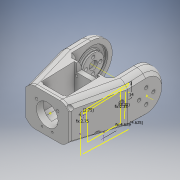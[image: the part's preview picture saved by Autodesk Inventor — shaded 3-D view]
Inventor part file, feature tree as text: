
AUTODESK INVENTOR PART (.ipt)
format: ipt  version: 2018 (Build 220112000, 112)  size: 1,030,656 bytes
history: native  units: mm
features: projected_geometry x48, sketch x44, extrude x36, hole x13, other x10, chamfer x9, fillet x7, reference x3, mirror x1, plane x1
ambient origin geometry x8: Origin, YZ Plane, XZ Plane, XY Plane, X Axis, Y Axis, Z Axis, Center Point
bodies: Solid1 (feature_tree)
feature tree (172):
  extrude  "Extrusion1"  Depth=45.0mm
  extrude  "Extrusion2"  Depth=2.25mm
  hole  "Hole1"  [1 undecoded]
  hole  "Hole2"  [1 undecoded]
  fillet  "Fillet1"  Radius=14.0mm
  extrude  "Extrusion3"  Depth=18.5mm
  extrude  "Extrusion4"  Depth=10.0mm
  extrude  "Extrusion5"  Depth=2.0mm
  extrude  "Extrusion6"  Depth=2.0mm
  hole  "Hole3"  [1 undecoded]
  extrude  "Extrusion7"  Depth=2.0mm
  extrude  "Extrusion8"  Depth=1.0mm TaperAngle=0.0deg
  extrude  "Extrusion9"  Depth=24.5mm
  extrude  "Extrusion10"  Depth=10.0mm
  extrude  "Extrusion11"  Depth=14.5mm
  extrude  "Extrusion13"  Depth=14.5mm
  extrude  "Extrusion14"  Depth=5.0mm
  extrude  "Extrusion15"  Depth=2.25mm
  extrude  "Extrusion16"  Depth=5.0mm
  extrude  "Extrusion17"  Depth=9.0mm
  chamfer  "Chamfer1"  Distance=1.0mm
  fillet  "Fillet7"  Radius=20.7mm
  fillet  "Fillet8"  Radius=32.0mm
  mirror  "Mirror1"
  sketch  "Sketch26"  dims[d55=2.25mm d56=5.0mm]
  extrude  "Extrusion24"  Depth=1.0mm TaperAngle=0.0deg
  extrude  "Extrusion25"  Depth=8.0mm
  extrude  "Extrusion26"  Depth=0.2mm TaperAngle=0.0deg
  extrude  "Extrusion27"  Depth=5.0mm TaperAngle=0.0deg
  other  "Work Axis1"
  plane  "Work Plane2"
  extrude  "Extrusion28"  Depth=0.2mm TaperAngle=0.0deg
  extrude  "Extrusion29"  Depth=2.0mm TaperAngle=45.0deg
  chamfer  "Chamfer2"  Distance=15.0mm
  extrude  "Extrusion31"  Depth=15.0mm TaperAngle=0.0deg
  chamfer  "Chamfer3"  Distance=15.0mm
  chamfer  "Chamfer4"  Distance=100.0mm
  extrude  "Extrusion32"  Depth=2.0mm TaperAngle=0.0deg
  chamfer  "Chamfer5"  Distance=6.0mm Angle=45.0deg
  extrude  "Extrusion33"  TaperAngle=0.0deg  [1 undecoded]
  sketch  "Sketch41"  dims[d100=0.2mm d101=0.0mm d102=2.5mm d103=2.0mm d104=45.0deg]
  extrude  "Extrusion34"  Depth=2.0mm
  chamfer  "Chamfer6"  Distance=11.5mm
  fillet  "Fillet9"  Radius=11.5mm
  extrude  "Extrusion35"  Depth=2.0mm TaperAngle=0.0deg
  extrude  "Extrusion36"  Depth=2.0mm TaperAngle=45.0deg
  chamfer  "Chamfer7"  Distance=2.0mm Angle=45.0deg
  fillet  "Fillet10"  Radius=7.0mm
  extrude  "Extrusion37"  Depth=2.0mm TaperAngle=0.0deg
  extrude  "Extrusion38"  Depth=2.0mm TaperAngle=45.0deg
  extrude  "Extrusion39"  Depth=2.0mm TaperAngle=0.0deg
  extrude  "Extrusion40"  Depth=2.0mm TaperAngle=0.0deg
  chamfer  "Chamfer8"  Distance=2.0mm Angle=45.0deg
  chamfer  "Chamfer9"  Distance=8.0mm
  hole  "Hole6"  [1 undecoded]
  fillet  "Fillet11"  Radius=10.970628mm
  fillet  "Fillet12"  Radius=15.470628mm
  extrude  "Extrusion41"  Depth=2.0mm TaperAngle=0.0deg
  extrude  "Extrusion42"  Depth=2.0mm TaperAngle=0.0deg
  hole  "Hole7"  [1 undecoded]
  extrude  "Extrusion43"  Depth=2.0mm
  extrude  "Extrusion44"  TaperAngle=15.0deg  [1 undecoded]
  sketch  "Sketch58"  dims[d162=5.0mm d165=100.0mm d166=0.0mm d167=100.0mm d168=0.0mm d169=6.0mm d170=2.0mm d171=45.0deg d172=0.0mm d173=11.5mm d175=11.5mm d176=11.5mm d179=100.0mm d180=0.0mm d181=5.0mm d182=2.0mm d183=45.0deg d184=5.0mm d185=2.0mm d186=45.0deg d187=7.0mm d188=100.0mm d189=0.0mm d190=5.0mm d191=2.0mm d192=45.0deg d193=100.0mm d194=0.0mm d195=100.0mm d196=0.0mm d197=5.0mm d198=2.0mm d199=45.0deg d200=8.0mm d202=15.0deg d204=10.970628mm d205=15.470628mm d206=2.5mm d207=0.0mm d208=2.5mm d209=0.0mm d210=3.0mm d211=2.0mm d212=45.0deg d213=2.0mm d215=15.0deg d216=4.0mm d217=4.0mm d218=5.0mm d219=0.0mm d222=32.0mm d223=4.0mm d224=0.0mm d225=2.5mm d226=0.0mm d227=6.5mm d228=0.0mm d229=3.0mm d230=2.0mm d231=45.0deg d232=3.0mm d233=2.0mm d234=45.0deg d235=1.567mm d236=15.0mm d237=4.0mm d238=2.0mm d239=90.0deg d240=15.0mm d241=20.594885mm d242=2.0mm d243=0.75mm d244=20.5mm d245=3.05mm d246=0.0mm d247=14.0mm d248=3.2mm d249=6.0mm d250=4.0mm d251=2.0mm d252=90.0deg d253=8.8mm d254=20.594885mm d255=20.5mm d256=1.55mm d257=0.0mm d258=8.0mm d259=2.5mm d260=0.0mm d261=8.0mm d262=2.5mm d263=0.0mm d266=4.624622mm d267=4.624622mm d268=2.75mm d269=2.75mm d270=2.35mm d271=2.35mm d272=14.0mm d273=4.0mm d274=5.6mm d275=3.708mm d276=3.023mm d277=2.0mm d278=14.3117mm d279=17.0mm d280=0.0mm d281=4.0mm d282=3.708mm d283=3.023mm d284=2.0mm d285=14.3117mm d286=19.0mm d287=0.0mm d288=4.0mm d289=3.708mm d290=3.023mm d291=2.0mm d292=14.3117mm d293=13.0mm d294=0.0mm d295=2.3mm d296=4.0mm d297=4.4mm d298=2.0mm d299=90.0deg d300=32.25mm d301=0.0mm d302=3.3mm d303=4.0mm d304=6.3mm d305=2.0mm d306=90.0deg d307=32.25mm d308=0.0mm d309=1.567mm d310=4.0mm d311=6.3mm d312=2.0mm d313=90.0deg d314=45.0mm d315=20.594885mm d316=1.567mm d317=4.0mm d318=6.3mm d319=2.0mm d320=90.0deg d321=55.0mm d322=20.594885mm d323=2.459mm d324=6.0mm d325=6.3mm d326=2.0mm d327=90.0deg d328=50.0mm d329=20.594885mm]
  hole  "Hole8"  [1 undecoded]
  hole  "Hole9"  [1 undecoded]
  hole  "Hole10"  [1 undecoded]
  hole  "Hole11"  [1 undecoded]
  hole  "Hole12"  [1 undecoded]
  hole  "Hole13"  [1 undecoded]
  hole  "Hole14"  [1 undecoded]
  hole  "Hole15"  [1 undecoded]
  sketch  "Sketch1"  dims[d0=24.5mm d1=45.0mm]
  sketch  "Sketch2"  dims[d2=1.95mm d3=0.0mm d4=2.25mm]
  projected_geometry  "Projected Loop1"
  sketch  "Sketch3"  dims[d5=20.0mm d6=2.25mm]
  projected_geometry  "Projected Loop2"
  sketch  "Sketch4"  dims[d7=5.25mm d8=5.25mm d9=14.0mm]
  projected_geometry  "Projected Loop3"
  sketch  "Sketch5"  dims[d10=5.25mm d11=18.5mm]
  projected_geometry  "Projected Loop4"
  sketch  "Sketch6"  dims[d12=10.0mm d13=0.0mm d14=20.5mm]
  projected_geometry  "Projected Loop5"
  sketch  "Sketch7"  dims[d15=2.0mm d16=2.195mm]
  projected_geometry  "Projected Loop6"
  sketch  "Sketch8"  dims[d17=2.0mm]
  projected_geometry  "Projected Loop7"
  sketch  "Sketch9"  dims[d18=2.4mm d19=6.0mm d20=4.4mm d21=2.0mm d22=90.0deg d23=8.0mm d24=20.594885mm d25=20.5mm]
  projected_geometry  "Projected Loop8"
  projected_geometry  "Projected Loop9"
  sketch  "Sketch10"  dims[d26=26.65mm d27=2.0mm]
  projected_geometry  "Projected Loop10"
  projected_geometry  "Projected Loop11"
  sketch  "Sketch11"  dims[d28=2.0mm]
  projected_geometry  "Projected Loop12"
  sketch  "Sketch12"  dims[d29=2.4mm d30=6.0mm d31=4.4mm d32=2.0mm d33=90.0deg d34=8.0mm d35=20.594885mm d36=0.5mm]
  sketch  "Sketch13"  dims[d37=18.0mm d38=1.0mm d39=0.0mm]
  sketch  "Sketch14"  dims[d41=5.0mm d42=0.0mm d43=24.5mm]
  projected_geometry  "Projected Loop13"
  sketch  "Sketch16"  dims[d44=1.15mm d45=0.0mm d46=10.0mm]
  projected_geometry  "Projected Loop14"
  sketch  "Sketch17"  dims[d47=21.0mm d48=14.5mm]
  projected_geometry  "Projected Loop15"
  sketch  "Sketch18"  dims[d49=20.0mm d50=14.5mm]
  projected_geometry  "Projected Loop16"
  sketch  "Sketch19"  dims[d51=24.5mm d52=5.0mm]
  projected_geometry  "Projected Loop17"
  sketch  "Sketch20"  dims[d53=5.0mm d54=2.25mm]
  projected_geometry  "Projected Loop18"
  projected_geometry  "Projected Loop25"
  sketch  "Sketch31"  dims[d57=5.0mm d58=9.0mm]
  projected_geometry  "Projected Loop30"
  reference  "Reference1"
  sketch  "Sketch32"  dims[d59=14.75mm]
  projected_geometry  "Projected Loop31"
  sketch  "Sketch33"  dims[d60=4.0mm d61=1.0mm d62=0.0mm d63=20.7mm]
  projected_geometry  "Projected Loop32"
  sketch  "Sketch34"  dims[d64=2.3mm d65=6.0mm d66=4.4mm d67=2.0mm d68=90.0deg d69=8.0mm d70=20.594885mm d72=32.0mm]
  projected_geometry  "Projected Loop33"
  other  "Work Point1"
  other  "Work Point2"
  other  "Work Point3"
  sketch  "Sketch35"  dims[d73=3.0mm d74=0.0mm d75=1.0mm d76=0.0mm]
  sketch  "Sketch37"  dims[d77=12.25mm d78=0.0mm d80=8.0mm]
  projected_geometry  "Projected Loop34"
  sketch  "Sketch38"  dims[d81=4.5mm d82=0.0mm d84=0.2mm d85=0.0mm]
  sketch  "Sketch39"  dims[d91=8.0mm d92=0.0mm d93=5.0mm d94=0.0mm]
  sketch  "Sketch40"  dims[d95=5.0mm d96=0.0mm d98=0.2mm d99=0.0mm]
  projected_geometry  "Projected Loop35"
  projected_geometry  "Projected Loop36"
  projected_geometry  "Projected Loop37"
  projected_geometry  "Projected Loop38"
  sketch  "Sketch42"  dims[d105=1.5mm]
  projected_geometry  "Projected Loop39"
  sketch  "Sketch43"  dims[d114=0.5mm]
  reference  "Reference2"
  reference  "Reference3"
  sketch  "Sketch45"  dims[d130=60.0mm]
  projected_geometry  "Projected Loop40"
  sketch  "Sketch46"  dims[d131=36.0mm]
  projected_geometry  "Projected Loop41"
  sketch  "Sketch48"  dims[d146=40.0mm]
  projected_geometry  "Projected Loop43"
  sketch  "Sketch49"  dims[d147=60.0mm]
  projected_geometry  "Projected Loop44"
  projected_geometry  "Projected Loop45"
  sketch  "Sketch50"  dims[d148=0.0mm]
  projected_geometry  "Projected Loop46"
  sketch  "Sketch52"  dims[d149=2.3mm d150=15.0mm d151=0.0mm]
  sketch  "Sketch53"  dims[d152=15.0mm d153=0.0mm d154=15.0mm d155=0.0mm d156=15.0mm d157=0.0mm]
  projected_geometry  "Projected Loop47"
  sketch  "Sketch54"  dims[d158=20.5mm]
  projected_geometry  "Projected Loop48"
  sketch  "Sketch55"  dims[d159=41.5mm]
  sketch  "Sketch56"  dims[d160=15.5mm]
  projected_geometry  "Projected Loop49"
  sketch  "Sketch57"  dims[d161=15.5mm]
  projected_geometry  "Projected Loop50"
  projected_geometry  "Projected Loop51"
  projected_geometry  "Projected Loop52"
  projected_geometry  "Projected Loop53"
  projected_geometry  "Projected Loop54"
  projected_geometry  "Projected Loop55"
  projected_geometry  "Projected Loop56"
  projected_geometry  "Projected Loop57"
  parser-record x1  (decoder bookkeeping rows leaked as tree rows — omitted from the tree; the rows remain in map.json)
  other  "servocheck.iam"
  other  "LX-16A:3"
  other  "DUOPAN-SG-SJ_10"
  projected_geometry  "Project Cut Edges1"
  projected_geometry  "Project Cut Edges3"
  other  "bottomarm:1"
  other  "arm1:1"
note: 15 required parameter values undecoded (feature->parameter linkage not recoverable at this tier; creation-order binding heuristic only, values carry confidence <= 0.55)
note: 1 file-system path scrubbed to <path> (originals preserved in map.json)
